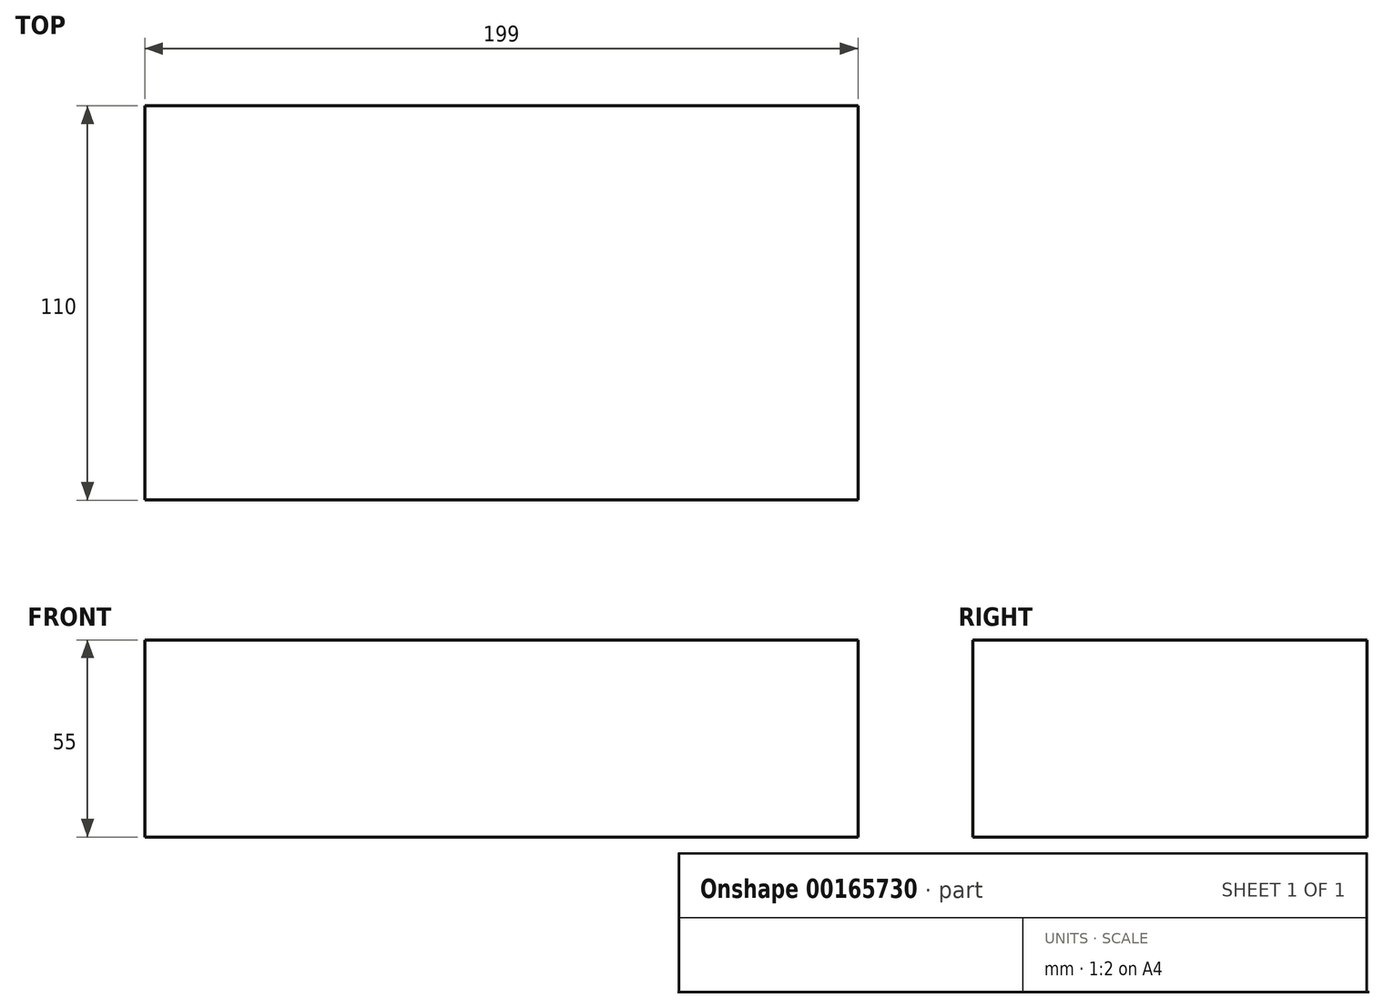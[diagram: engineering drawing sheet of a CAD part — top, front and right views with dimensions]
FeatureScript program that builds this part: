
annotation { "Feature Type Name" : "Feature", "Feature Type Description" : "" }
export const myFeature = defineFeature(function(context is Context, id is Id, definition is map)
    precondition{}
    {
        {
            var Q0;
            Q0=qCreatedBy(makeId("Top.planeOp"),FACE);
            var sketch = newSketch(context, id + "F0", { "sketchPlane" : qUnion([Q0])});
            skLineSegment(sketch, "E0.bottom", {"start": v(-99.2, 58.7) * mm, "end": v(99.8, 58.7) * mm});
            skLineSegment(sketch, "E0.top", {"start": v(-99.2, -51.3) * mm, "end": v(99.8, -51.3) * mm});
            skLineSegment(sketch, "E0.left", {"start": v(-99.2, 58.7) * mm, "end": v(-99.2, -51.3) * mm});
            skLineSegment(sketch, "E0.right", {"start": v(99.8, 58.7) * mm, "end": v(99.8, -51.3) * mm});
            skSolve(sketch);
        }
        {
            var Q0;
            Q0=makeQuery(id+"F0.imprint","IMPRINT",FACE,{"disambiguationData":[TD([[makeQuery(id+"F0.imprint","IMPRINT",EDGE,{"derivedFrom":sQuery(id+"F0.wireOp",EDGE,"E0.bottom")}),-1.0]])]});
            extrude(context, id + "F1", {"entities" : qUnion([Q0]), "depth" : 55 * mm});
        }
    });
